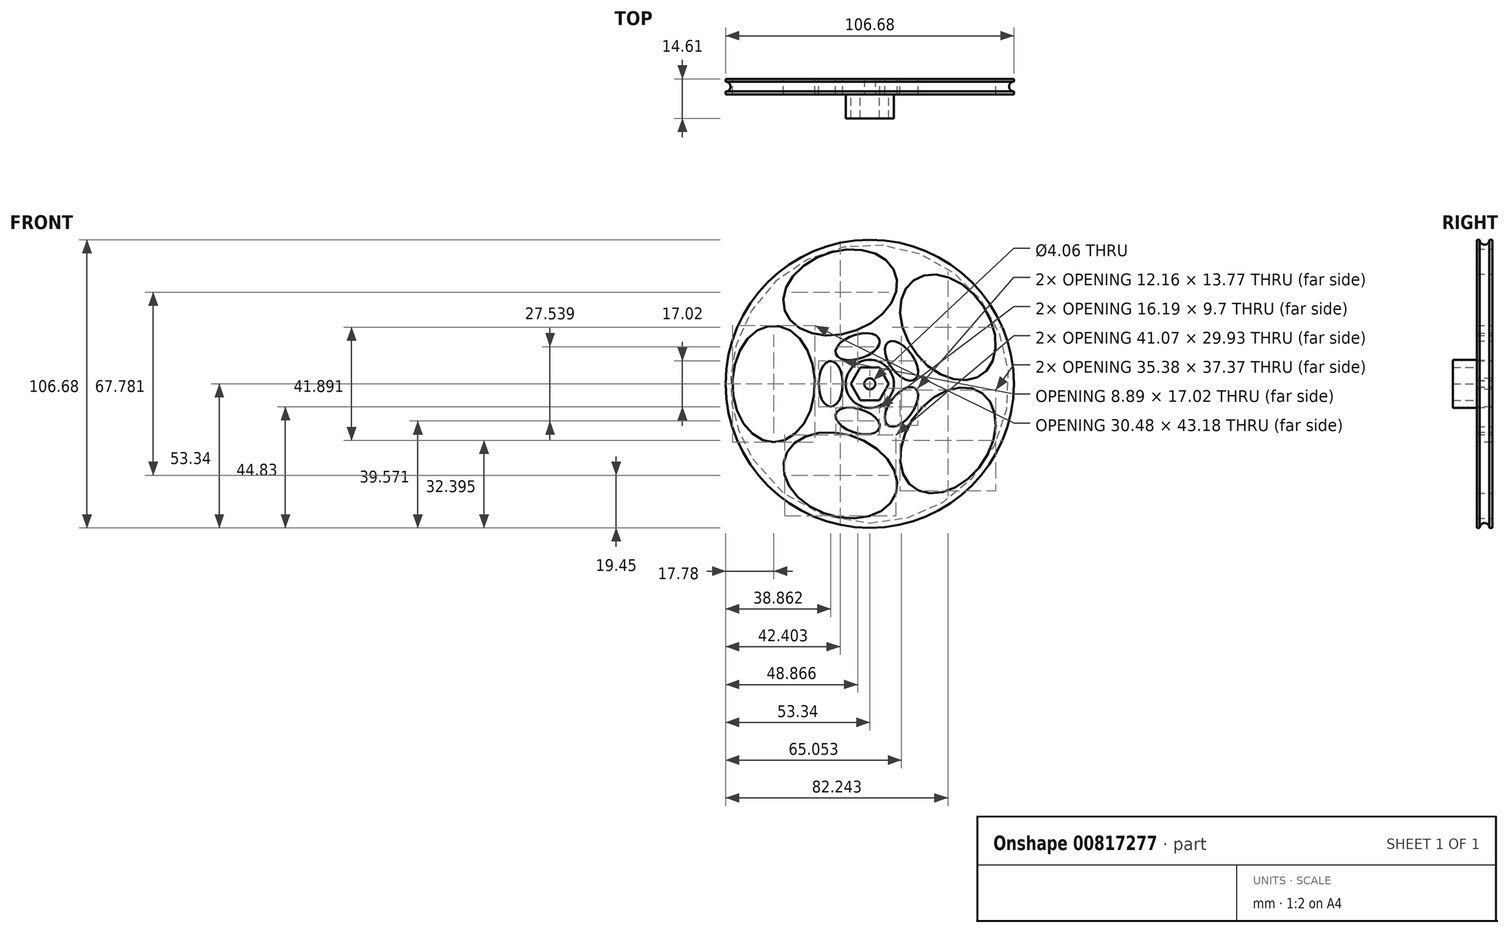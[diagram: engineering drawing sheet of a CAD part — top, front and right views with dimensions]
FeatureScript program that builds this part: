
annotation { "Feature Type Name" : "Feature", "Feature Type Description" : "" }
export const myFeature = defineFeature(function(context is Context, id is Id, definition is map)
    precondition{}
    {
        {
            var Q0;
            Q0=qCreatedBy(makeId("Front.planeOp"),FACE);
            var sketch = newSketch(context, id + "F0", { "sketchPlane" : qUnion([Q0])});
            skCircle(sketch, "E0", {"center": v(0, 0) * mm, "radius": 53.34 * mm});
            skSolve(sketch);
        }
        {
            var Q0;
            Q0 = qSketchRegion(id + "F0", true);
            extrude(context, id + "F1", {"entities" : qUnion([Q0]), "depth" : 5.7 * mm, "offsetDistance" : 25.4 * mm, "symmetric" : true});
        }
        {
            var Q0;
            Q0=makeQuery(id+"F1.opExtrude","CAP_FACE",FACE,{"disambiguationData":[OSD([sQuery(id+"F0.wireOp",EDGE,"E0")])],"isStart":false});
            var sketch = newSketch(context, id + "F2", { "sketchPlane" : qUnion([Q0])});
            skLineSegment(sketch, "E1.0", {"start": v(-3.52, 6.1) * mm, "end": v(3.52, 6.1) * mm});
            skLineSegment(sketch, "E1.1", {"start": v(3.52, 6.1) * mm, "end": v(7.04, 0) * mm});
            skLineSegment(sketch, "E1.2", {"start": v(7.04, 0) * mm, "end": v(3.52, -6.1) * mm});
            skLineSegment(sketch, "E1.3", {"start": v(3.52, -6.1) * mm, "end": v(-3.52, -6.1) * mm});
            skLineSegment(sketch, "E1.4", {"start": v(-3.52, -6.1) * mm, "end": v(-7.04, 0) * mm});
            skLineSegment(sketch, "E1.5", {"start": v(-7.04, 0) * mm, "end": v(-3.52, 6.1) * mm});
            skPoint(sketch, "E1.0.midPoint", {"position": v(0, 6.1) * mm});
            skPoint(sketch, "E1.cCircle.center.orphan", {"position": v(0, 0) * mm});
            skCircle(sketch, "E2", {"center": v(0, 0) * mm, "radius": 8.9 * mm});
            skSolve(sketch);
        }
        {
            var Q0;
            Q0 = qSketchRegion(id + "F2", true);
            extrude(context, id + "F3", {"entities" : qUnion([Q0]), "operationType" : NewBodyOperationType.ADD, "depth" : 8.9 * mm, "offsetDistance" : 25.4 * mm});
        }
        {
            var Q0;
            Q0=makeQuery(id+"F3.boolean.opBoolean","SPLIT",FACE,{"disambiguationData":[TD([makeQuery(id+"F3.opExtrude","SWEPT_FACE",FACE,{"disambiguationData":[OSD([sQuery(id+"F2.wireOp",EDGE,"E1.0")])]})])],"derivedFrom":makeQuery(id+"F1.opExtrude","CAP_FACE",FACE,{"disambiguationData":[OSD([sQuery(id+"F0.wireOp",EDGE,"E0")])],"isStart":false})});
            var sketch = newSketch(context, id + "F4", { "sketchPlane" : qUnion([Q0])});
            skCircle(sketch, "E3", {"center": v(0, 0) * mm, "radius": 2.03 * mm});
            skSolve(sketch);
        }
        {
            var Q0;
            Q0 = qSketchRegion(id + "F4", true);
            extrude(context, id + "F5", {"entities" : qUnion([Q0]), "operationType" : NewBodyOperationType.REMOVE, "endBound" : BoundingType.UP_TO_NEXT, "oppositeDirection" : true, "depth" : 25.4 * mm, "offsetDistance" : 25.4 * mm});
        }
        {
            var Q0;
            {var subQ0=sQuery(id+"F0.wireOp",EDGE,"E0");Q0=makeQuery(id+"F3.boolean.opBoolean","SPLIT",FACE,{"disambiguationData":[TD([makeQuery(id+"F1.opExtrude","SWEPT_FACE",FACE,{"disambiguationData":[OSD([subQ0])]})])],"derivedFrom":makeQuery(id+"F1.opExtrude","CAP_FACE",FACE,{"disambiguationData":[OSD([subQ0])],"isStart":false})});}
            var sketch = newSketch(context, id + "F6", { "sketchPlane" : qUnion([Q0])});
            skEllipse(sketch, "E4", {"center": v(-35.56, 0) * mm, "majorRadius": 21.59 * mm, "minorRadius": 15.24 * mm, "majorAxis": v(0, -1)});
            skEllipse(sketch, "E5.1.0", {"center": v(-10.94, -33.9) * mm, "majorRadius": 21.59 * mm, "minorRadius": 15.24 * mm, "majorAxis": v(0.95, -0.3)});
            skEllipse(sketch, "E5.2.0", {"center": v(28.9, -20.95) * mm, "majorRadius": 21.59 * mm, "minorRadius": 15.24 * mm, "majorAxis": v(0.59, 0.8)});
            skEllipse(sketch, "E5.3.0", {"center": v(28.9, 20.95) * mm, "majorRadius": 21.59 * mm, "minorRadius": 15.24 * mm, "majorAxis": v(-0.59, 0.8)});
            skEllipse(sketch, "E5.4.0", {"center": v(-10.94, 33.9) * mm, "majorRadius": 21.59 * mm, "minorRadius": 15.24 * mm, "majorAxis": v(-0.95, -0.3)});
            skPoint(sketch, "E5.center", {"position": v(0.07, 0) * mm});
            skEllipse(sketch, "E6", {"center": v(-14.48, 0) * mm, "majorRadius": 8.5 * mm, "minorRadius": 4.45 * mm, "majorAxis": v(0, -1)});
            skEllipse(sketch, "E7.1.0", {"center": v(-4.47, -13.77) * mm, "majorRadius": 8.5 * mm, "minorRadius": 4.45 * mm, "majorAxis": v(0.95, -0.3)});
            skEllipse(sketch, "E7.2.0", {"center": v(11.71, -8.5) * mm, "majorRadius": 8.5 * mm, "minorRadius": 4.45 * mm, "majorAxis": v(0.59, 0.8)});
            skEllipse(sketch, "E7.3.0", {"center": v(11.71, 8.5) * mm, "majorRadius": 8.5 * mm, "minorRadius": 4.45 * mm, "majorAxis": v(-0.59, 0.8)});
            skEllipse(sketch, "E7.4.0", {"center": v(-4.47, 13.77) * mm, "majorRadius": 8.5 * mm, "minorRadius": 4.45 * mm, "majorAxis": v(-0.95, -0.3)});
            skPoint(sketch, "E7.center", {"position": v(0, 0) * mm});
            skSolve(sketch);
        }
        {
            var Q0;
            Q0 = qSketchRegion(id + "F6", true);
            extrude(context, id + "F7", {"entities" : qUnion([Q0]), "operationType" : NewBodyOperationType.REMOVE, "oppositeDirection" : true, "depth" : 25.4 * mm, "offsetDistance" : 25.4 * mm, "symmetric" : true});
        }
        {
            var Q0;
            Q0=qCreatedBy(makeId("Right.planeOp"),FACE);
            var sketch = newSketch(context, id + "F8", { "sketchPlane" : qUnion([Q0])});
            skCircle(sketch, "E8", {"center": v(0, 53.34) * mm, "radius": 1.8 * mm});
            skSolve(sketch);
        }
        {
            var Q0;
            Q0=qCreatedBy(makeId("Top.planeOp"),FACE);
            var sketch = newSketch(context, id + "F9", { "sketchPlane" : qUnion([Q0])});
            skLineSegment(sketch, "E9", {"start": v(0, 0) * mm, "end": v(0, -38.66) * mm});
            skSolve(sketch);
        }
        {
            var Q0;
            Q0 = qSketchRegion(id + "F8", true);
            var Q1;
            Q1=sQuery(id+"F9.wireOp",EDGE,"E9");
            revolve(context, id + "F10", {"operationType" : NewBodyOperationType.REMOVE, "surfaceOperationType" : NewSurfaceOperationType.NEW, "entities" : qUnion([Q0]), "axis" : qUnion([Q1]), "revolveType" : RevolveType.FULL, "oppositeDirection" : true});
        }
    });
